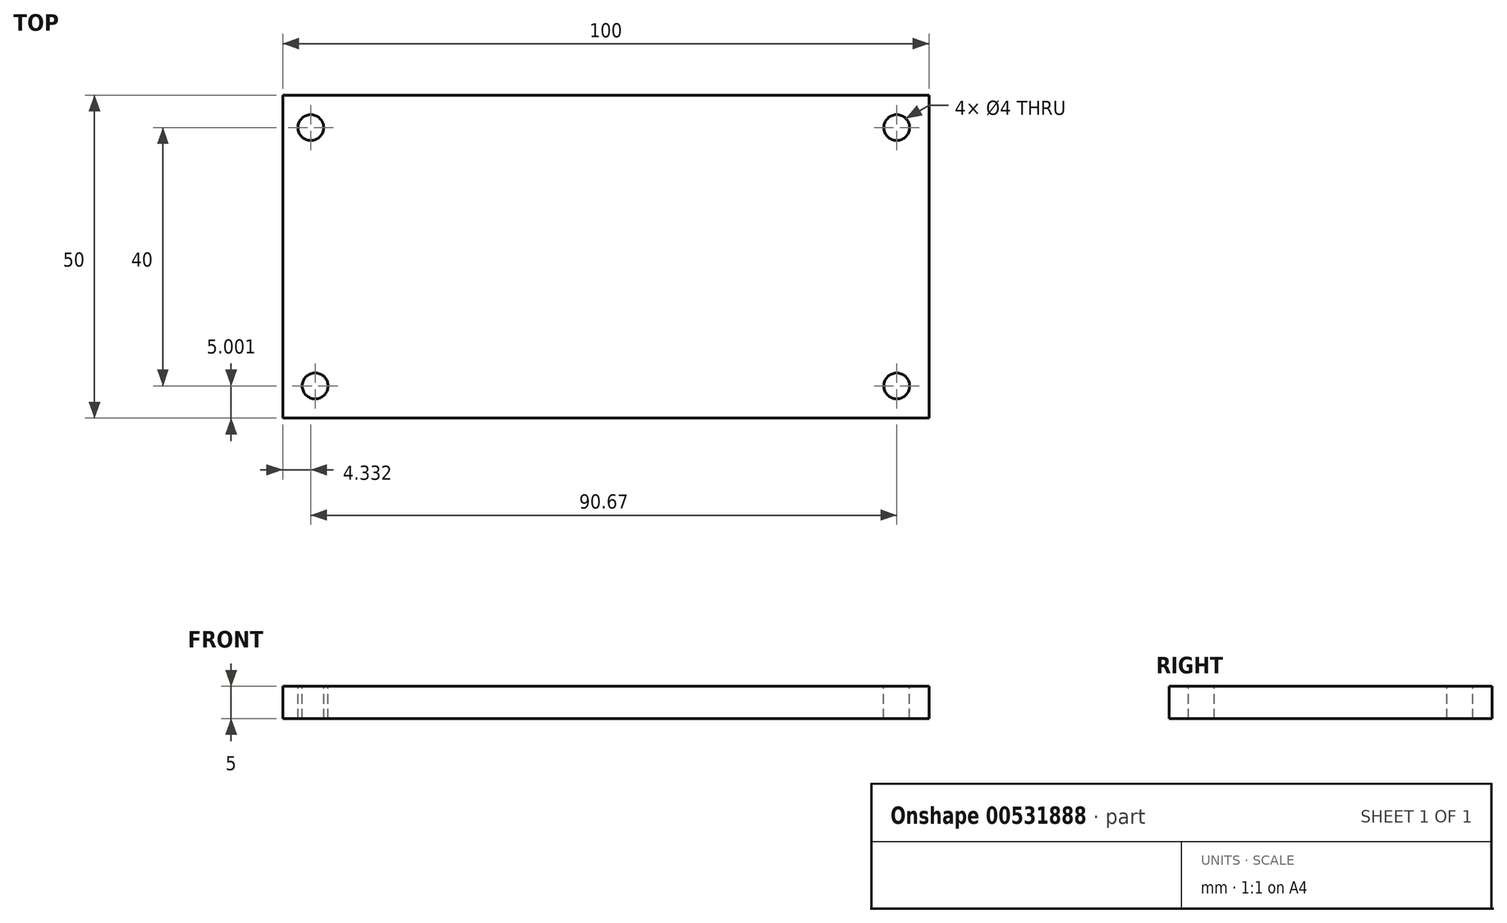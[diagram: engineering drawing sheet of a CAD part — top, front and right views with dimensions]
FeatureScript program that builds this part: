
annotation { "Feature Type Name" : "Feature", "Feature Type Description" : "" }
export const myFeature = defineFeature(function(context is Context, id is Id, definition is map)
    precondition{}
    {
        {
            var Q0;
            Q0=qCreatedBy(makeId("Top.planeOp"),FACE);
            var sketch = newSketch(context, id + "F0", { "sketchPlane" : qUnion([Q0])});
            skLineSegment(sketch, "E0.bottom", {"start": v(-53.55, 21.33) * mm, "end": v(46.45, 21.33) * mm});
            skLineSegment(sketch, "E0.top", {"start": v(-53.55, -28.67) * mm, "end": v(46.45, -28.67) * mm});
            skLineSegment(sketch, "E0.left", {"start": v(-53.55, 21.33) * mm, "end": v(-53.55, -28.67) * mm});
            skLineSegment(sketch, "E0.right", {"start": v(46.45, 21.33) * mm, "end": v(46.45, -28.67) * mm});
            skSolve(sketch);
        }
        {
            var Q0;
            Q0 = qSketchRegion(id + "F0", true);
            extrude(context, id + "F1", {"entities" : qUnion([Q0]), "depth" : 5 * mm, "offsetDistance" : 25 * mm});
        }
        {
            var Q0;
            Q0=makeQuery(id+"F1.opExtrude","CAP_FACE",FACE,{"disambiguationData":[OSD([sQuery(id+"F0.wireOp",EDGE,"E0.bottom"),sQuery(id+"F0.wireOp",EDGE,"E0.top"),sQuery(id+"F0.wireOp",EDGE,"E0.left"),sQuery(id+"F0.wireOp",EDGE,"E0.right")])],"isStart":false});
            var sketch = newSketch(context, id + "F2", { "sketchPlane" : qUnion([Q0])});
            skLineSegment(sketch, "E1", {"start": v(-53.55, 21.33) * mm, "end": v(-53.55, 18.83) * mm});
            skCircle(sketch, "E2", {"center": v(-49.22, 16.33) * mm, "radius": 2 * mm});
            skCircle(sketch, "E3", {"center": v(41.45, 16.33) * mm, "radius": 2 * mm});
            skCircle(sketch, "E4", {"center": v(-48.55, -23.67) * mm, "radius": 2 * mm});
            skLineSegment(sketch, "E5", {"start": v(38.95, -23.67) * mm, "end": v(41.45, -23.67) * mm});
            skCircle(sketch, "E6", {"center": v(41.45, -23.67) * mm, "radius": 2 * mm});
            skSolve(sketch);
        }
        {
            var Q0;
            Q0 = qSketchRegion(id + "F2", true);
            extrude(context, id + "F3", {"entities" : qUnion([Q0]), "operationType" : NewBodyOperationType.REMOVE, "oppositeDirection" : true, "depth" : 5 * mm, "offsetDistance" : 25 * mm});
        }
    });
